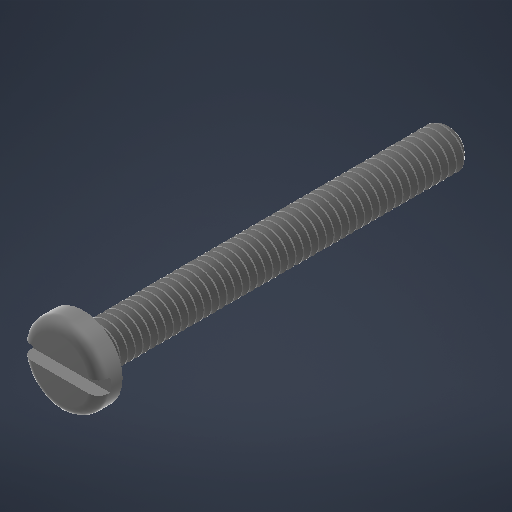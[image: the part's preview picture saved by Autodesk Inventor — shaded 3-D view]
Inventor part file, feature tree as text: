
AUTODESK INVENTOR PART (.ipt)
format: ipt  version: 2025.2 (Build 292293000, 293)  size: 679,936 bytes
history: native  units: in
note: dims shown in document units (in); Inventor stores cm internally (conversion verified against a paired STEP export)
features: other x1, extrude x1
ambient origin geometry x8: Origin, YZ Plane, XZ Plane, XY Plane, X Axis, Y Axis, Z Axis, Center Point
bodies: Solid1 (feature_tree)
feature tree (2):
  other  "Plane1"
  extrude  "Extrude15"  [1 undecoded]
note: 1 required parameter value undecoded (feature->parameter linkage not recoverable at this tier; creation-order binding heuristic only, values carry confidence <= 0.55)
